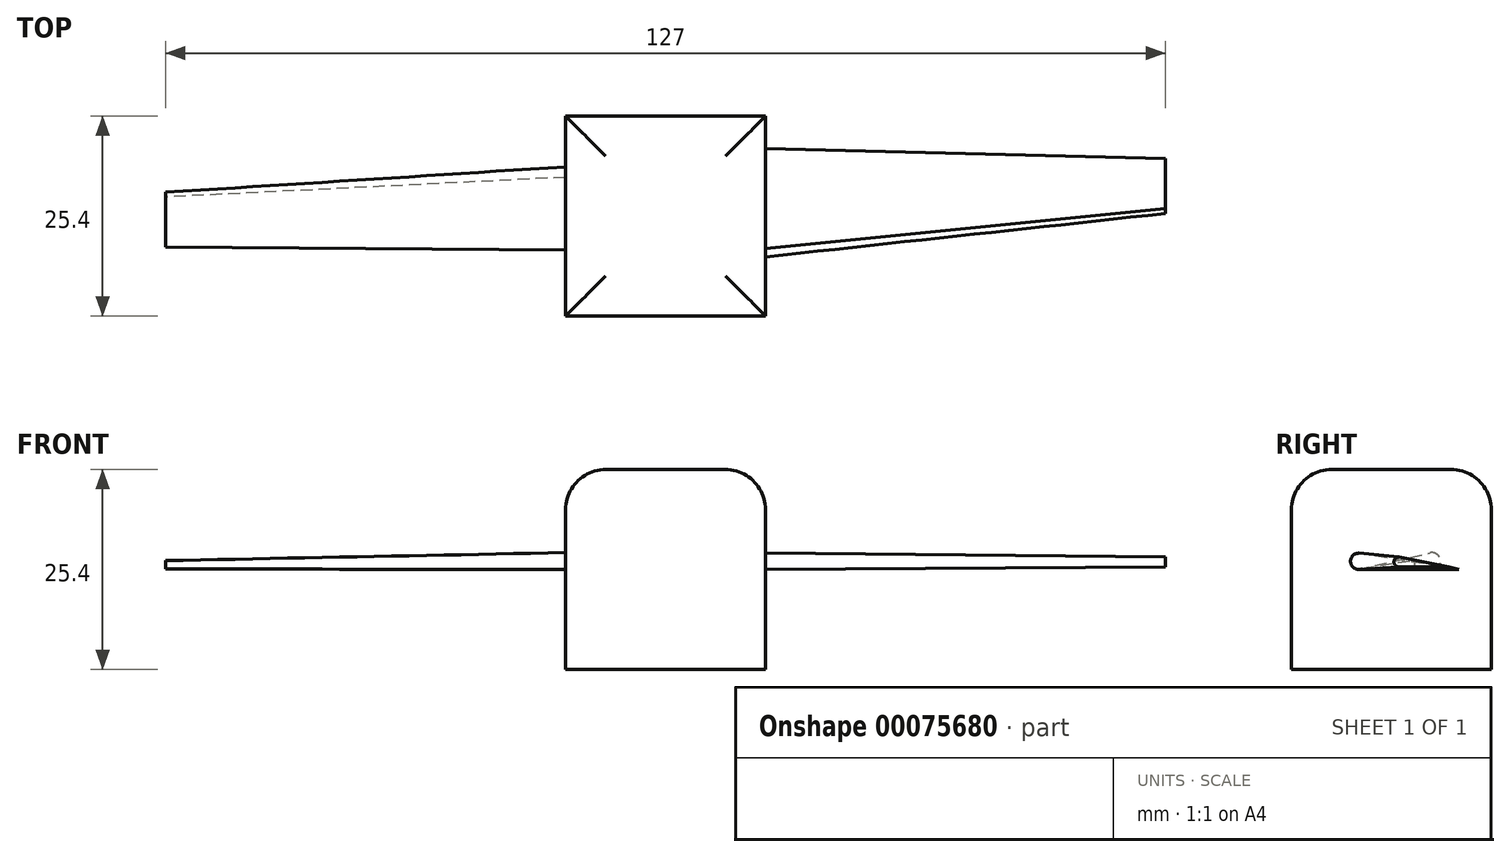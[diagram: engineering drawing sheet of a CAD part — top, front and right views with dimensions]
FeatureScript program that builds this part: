
annotation { "Feature Type Name" : "Feature", "Feature Type Description" : "" }
export const myFeature = defineFeature(function(context is Context, id is Id, definition is map)
    precondition{}
    {
        {
            var Q0;
            Q0=qCreatedBy(makeId("Front.planeOp"),FACE);
            var sketch = newSketch(context, id + "F0", { "sketchPlane" : qUnion([Q0])});
            skLineSegment(sketch, "E0.bottom", {"start": v(0, 0) * mm, "end": v(25.4, 0) * mm});
            skLineSegment(sketch, "E0.top", {"start": v(0, 25.4) * mm, "end": v(25.4, 25.4) * mm});
            skLineSegment(sketch, "E0.left", {"start": v(0, 0) * mm, "end": v(0, 25.4) * mm});
            skLineSegment(sketch, "E0.right", {"start": v(25.4, 0) * mm, "end": v(25.4, 25.4) * mm});
            skSolve(sketch);
        }
        {
            var Q0;
            Q0=makeQuery(id+"F0.imprint","IMPRINT",FACE,{"disambiguationData":[TD([[makeQuery(id+"F0.imprint","IMPRINT",EDGE,{"derivedFrom":sQuery(id+"F0.wireOp",EDGE,"E0.bottom")}),1.0]])]});
            extrude(context, id + "F1", {"entities" : qUnion([Q0]), "depth" : 25.4 * mm});
        }
        {
            var Q0;
            Q0=makeQuery(id+"F1.opExtrude","SWEPT_FACE",FACE,{"disambiguationData":[OSD([sQuery(id+"F0.wireOp",EDGE,"E0.right")])]});
            var sketch = newSketch(context, id + "F2", { "sketchPlane" : qUnion([Q0])});
            skLineSegment(sketch, "E1", {"start": v(-4.15, 12.7) * mm, "end": v(-16.85, 12.7) * mm});
            skPoint(sketch, "E1.startSnap0", {"position": v(0, 12.7) * mm});
            skLineSegment(sketch, "E2", {"start": v(-4.15, 12.7) * mm, "end": v(-16.85, 14.77) * mm});
            skArc(sketch, "E3", {"start": v(-16.85, 14.77) * mm, "mid": v(-17.89, 13.74) * mm, "end": v(-16.85, 12.7) * mm});
            skSolve(sketch);
        }
        {
            var Q0;
            Q0=makeQuery(id+"F2.imprint","IMPRINT",FACE,{"disambiguationData":[TD([[makeQuery(id+"F2.imprint","IMPRINT",EDGE,{"derivedFrom":sQuery(id+"F2.wireOp",EDGE,"E1")}),1.0]])]});
            cPlane(context, id + "F3", {"entities" : qUnion([Q0]), "cplaneType" : CPlaneType.OFFSET, "offset" : 50.8 * mm, "width" : 152.4 * mm, "height" : 152.4 * mm});
        }
        {
            var Q0;
            Q0=qCreatedBy(id+"F3.planeOp",FACE);
            var sketch = newSketch(context, id + "F4", { "sketchPlane" : qUnion([Q0])});
            skLineSegment(sketch, "E4", {"start": v(-5.4, 13.04) * mm, "end": v(-11.75, 13.04) * mm});
            skLineSegment(sketch, "E5", {"start": v(-5.4, 13.04) * mm, "end": v(-11.75, 14.28) * mm});
            skArc(sketch, "E6", {"start": v(-11.75, 14.28) * mm, "mid": v(-12.37, 13.66) * mm, "end": v(-11.75, 13.04) * mm});
            skSolve(sketch);
        }
        {
            var Q1;
            Q1=makeQuery(id+"F2.imprint","IMPRINT",FACE,{"disambiguationData":[TD([[makeQuery(id+"F2.imprint","IMPRINT",EDGE,{"derivedFrom":sQuery(id+"F2.wireOp",EDGE,"E1")}),-1.0]])]});
            var Q2;
            Q2=makeQuery(id+"F4.imprint","IMPRINT",FACE,{"disambiguationData":[TD([[makeQuery(id+"F4.imprint","IMPRINT",EDGE,{"derivedFrom":sQuery(id+"F4.wireOp",EDGE,"E4")}),-1.0]])]});
            loft(context, id + "F5", {"operationType" : NewBodyOperationType.ADD, "sheetProfilesArray" : [{ "sheetProfileEntities" : qUnion([Q1]) }, { "sheetProfileEntities" : qUnion([Q2]) }]});
        }
        {
            var Q0;
            Q0=makeQuery(id+"F1.opExtrude","SWEPT_FACE",FACE,{"disambiguationData":[OSD([sQuery(id+"F0.wireOp",EDGE,"E0.left")])]});
            var sketch = newSketch(context, id + "F6", { "sketchPlane" : qUnion([Q0])});
            skLineSegment(sketch, "E7", {"start": v(17.04, 12.7) * mm, "end": v(7.78, 12.7) * mm});
            skPoint(sketch, "E7.startSnap0", {"position": v(25.4, 12.7) * mm});
            skLineSegment(sketch, "E8", {"start": v(17.04, 12.7) * mm, "end": v(7.78, 14.81) * mm});
            skArc(sketch, "E9", {"start": v(7.78, 14.81) * mm, "mid": v(6.46, 13.76) * mm, "end": v(7.78, 12.7) * mm});
            skSolve(sketch);
        }
        {
            var Q0;
            Q0=makeQuery(id+"F6.imprint","IMPRINT",FACE,{"disambiguationData":[TD([[makeQuery(id+"F6.imprint","IMPRINT",EDGE,{"derivedFrom":sQuery(id+"F6.wireOp",EDGE,"E7")}),1.0]])]});
            cPlane(context, id + "F7", {"entities" : qUnion([Q0]), "cplaneType" : CPlaneType.OFFSET, "offset" : 50.8 * mm, "width" : 152.4 * mm, "height" : 152.4 * mm});
        }
        {
            var Q0;
            Q0=qCreatedBy(id+"F7.planeOp",FACE);
            var sketch = newSketch(context, id + "F8", { "sketchPlane" : qUnion([Q0])});
            skLineSegment(sketch, "E10", {"start": v(16.64, 12.79) * mm, "end": v(10.29, 12.79) * mm});
            skLineSegment(sketch, "E11", {"start": v(16.64, 12.79) * mm, "end": v(10.29, 13.82) * mm});
            skArc(sketch, "E12", {"start": v(10.29, 13.82) * mm, "mid": v(9.68, 13.3) * mm, "end": v(10.29, 12.79) * mm});
            skSolve(sketch);
        }
        {
            var Q1;
            Q1=makeQuery(id+"F6.imprint","IMPRINT",FACE,{"disambiguationData":[TD([[makeQuery(id+"F6.imprint","IMPRINT",EDGE,{"derivedFrom":sQuery(id+"F6.wireOp",EDGE,"E7")}),-1.0]])]});
            var Q2;
            Q2=makeQuery(id+"F8.imprint","IMPRINT",FACE,{"disambiguationData":[TD([[makeQuery(id+"F8.imprint","IMPRINT",EDGE,{"derivedFrom":sQuery(id+"F8.wireOp",EDGE,"E10")}),-1.0]])]});
            loft(context, id + "F9", {"operationType" : NewBodyOperationType.ADD, "sheetProfilesArray" : [{ "sheetProfileEntities" : qUnion([Q1]) }, { "sheetProfileEntities" : qUnion([Q2]) }]});
        }
        {
            var Q0;
            Q0=makeQuery(id+"F1.opExtrude","CAP_EDGE",EDGE,{"disambiguationData":[OSD([sQuery(id+"F0.wireOp",EDGE,"E0.top")])],"isStart":false});
            var Q1;
            Q1=makeQuery(id+"F1.opExtrude","SWEPT_EDGE",EDGE,{"disambiguationData":[OSD([sQuery(id+"F0.wireOp",EDGE,"E0.top"),sQuery(id+"F0.wireOp",EDGE,"E0.right")])]});
            var Q2;
            Q2=makeQuery(id+"F1.opExtrude","CAP_EDGE",EDGE,{"disambiguationData":[OSD([sQuery(id+"F0.wireOp",EDGE,"E0.top")])],"isStart":true});
            var Q3;
            Q3=makeQuery(id+"F1.opExtrude","SWEPT_EDGE",EDGE,{"disambiguationData":[OSD([sQuery(id+"F0.wireOp",EDGE,"E0.top"),sQuery(id+"F0.wireOp",EDGE,"E0.left")])]});
            fillet(context, id + "F10", {"entities" : qUnion([Q0, Q1, Q2, Q3]), "radius" : 5.08 * mm, "tangentPropagation" : true, "allowEdgeOverflow" : false});
        }
    });
